# Revit family: Potential- und Erdanschlussblock VA
name_source: partatom
category: Generic Models
revit_build: Autodesk Revit 2015 (Build: 20140606_1530(x64)
units: mm (PartAtom-declared; Revit-internal decimal feet)

## types (3) — shared parameters
Height = 55 mm  [stored 0.180446 ft]
Manufacturer = OBO Bettermann
Material = Stainless Steel
URL = http://www.obo-bettermann.com
Width = 50 mm  [stored 0.164042 ft]

## per-type parameters (varying)
| type | GTIN | Length | Length 1 | Manufacturer Art.No. |
| 1805 2 VA | 4012195922216 | 110 mm  [stored 0.360892 ft] | 200 mm  [stored 0.656168 ft] | 5016096 |
| 1805 4 VA | 4012195800354 | 212 mm  [stored 0.695538 ft] | 302 mm  [stored 0.990814 ft] | 5016118 |
| 1805 6 VA | 4012195922278 | 314 mm  [stored 1.03018 ft] | 404 mm  [stored 1.32546 ft] | 5016126 |

note: column(s) folded — value = type name in every type: Article Type

note: [stored X ft] marks values corroborated as IEEE doubles in the binary element streams (Revit-internal decimal feet)

## geometry (parser evidence)
native form markers: Sweep x1
no freeform markers — native parametric forms only
